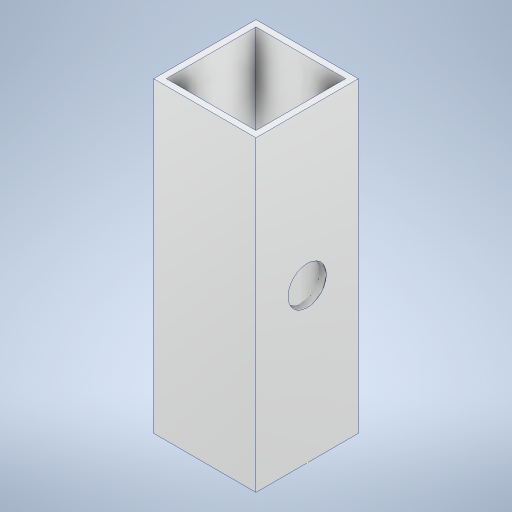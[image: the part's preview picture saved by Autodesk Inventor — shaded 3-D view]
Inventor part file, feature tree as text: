
AUTODESK INVENTOR PART (.ipt)
format: ipt  version: 2024 (Build 280153000, 153)  size: 285,184 bytes
history: native  units: mm
features: extrude x5, sketch x5, projected_geometry x1
ambient origin geometry x8: Origin, YZ Plane, XZ Plane, XY Plane, X Axis, Y Axis, Z Axis, Center Point
bodies: Solid1 (feature_tree)
feature tree (11):
  extrude  "Extrusion1"  Depth=25.4mm
  extrude  "Extrusion2"  Depth=1.5875mm
  extrude  "Extrusion3"  Depth=38.1mm
  sketch  "Sketch4"  dims[d4=660.4mm d5=0.0mm d6=38.1mm]
  extrude  "Extrusion4"  Depth=8.73125mm
  extrude  "Extrusion5"  Depth=177.8mm
  sketch  "Sketch2"  dims[d0=25.4mm d1=25.4mm]
  sketch  "Sketch3"  dims[d2=1.5875mm d3=1.5875mm]
  sketch  "Sketch5"  dims[d7=9.525mm d8=8.73125mm]
  sketch  "Sketch6"  dims[d9=46.600008mm d10=0.0mm d11=177.8mm d12=354.849999mm d13=0.0mm d14=114.3mm d15=40.850007mm d16=0.0mm d17=38.1mm d18=0.0mm]
  projected_geometry  "Projected Loop1"
